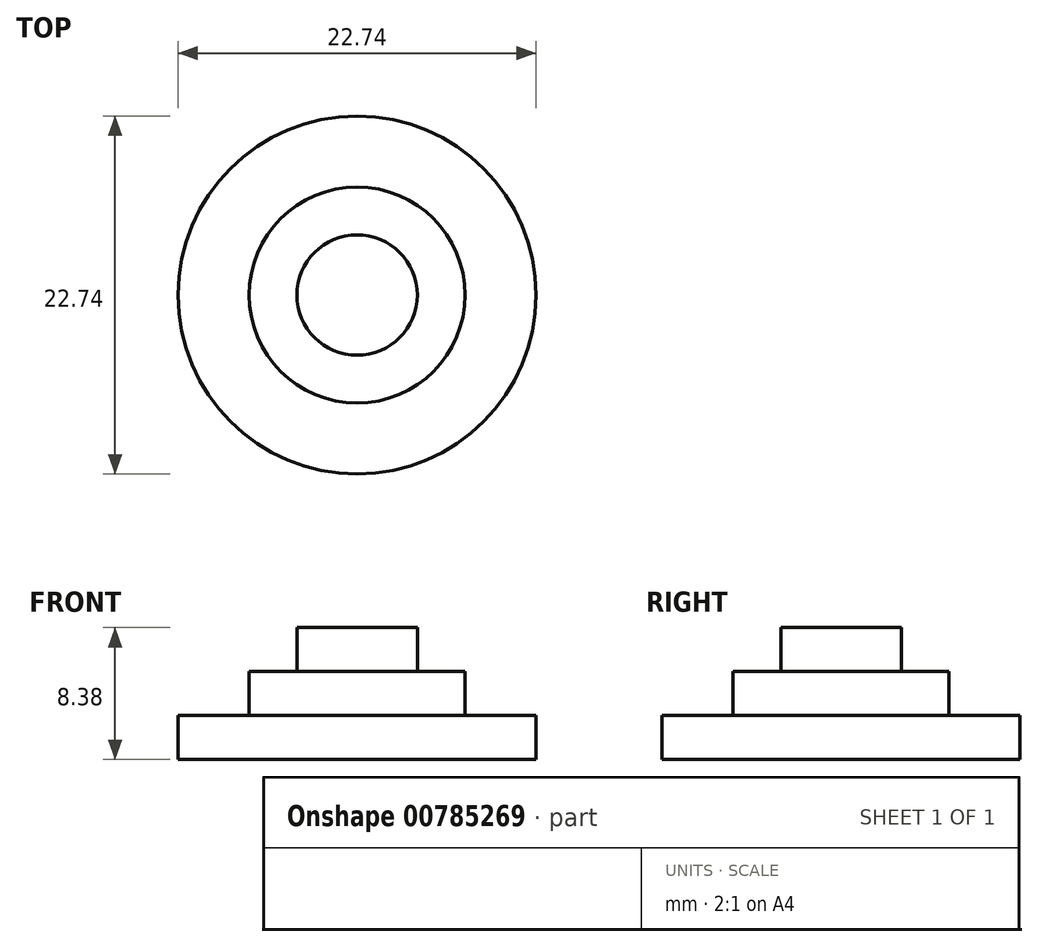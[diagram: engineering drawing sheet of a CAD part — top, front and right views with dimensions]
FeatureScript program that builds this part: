
annotation { "Feature Type Name" : "Feature", "Feature Type Description" : "" }
export const myFeature = defineFeature(function(context is Context, id is Id, definition is map)
    precondition{}
    {
        {
            var Q0;
            Q0=qCreatedBy(makeId("Top.planeOp"),FACE);
            var sketch = newSketch(context, id + "F0", { "sketchPlane" : qUnion([Q0])});
            skCircle(sketch, "E0", {"center": v(0, 0) * mm, "radius": 3.82 * mm});
            skCircle(sketch, "E1", {"center": v(0, 0) * mm, "radius": 6.86 * mm});
            skSolve(sketch);
        }
        {
            var Q0;
            Q0=makeQuery(id+"F0.imprint","IMPRINT",FACE,{"disambiguationData":[TD([[makeQuery(id+"F0.imprint","IMPRINT",EDGE,{"derivedFrom":sQuery(id+"F0.wireOp",EDGE,"E0")}),1.0]])]});
            extrude(context, id + "F1", {"entities" : qUnion([Q0]), "depth" : 2.8 * mm, "offsetDistance" : 25.4 * mm});
        }
        {
            var Q0;
            Q0=makeQuery(id+"F0.imprint","IMPRINT",FACE,{"disambiguationData":[TD([[makeQuery(id+"F0.imprint","IMPRINT",EDGE,{"derivedFrom":sQuery(id+"F0.wireOp",EDGE,"E0")}),-1.0]])]});
            var Q1;
            Q1=makeQuery(id+"F0.imprint","IMPRINT",FACE,{"disambiguationData":[TD([[makeQuery(id+"F0.imprint","IMPRINT",EDGE,{"derivedFrom":sQuery(id+"F0.wireOp",EDGE,"E0")}),1.0]])]});
            extrude(context, id + "F2", {"entities" : qUnion([Q0, Q1]), "operationType" : NewBodyOperationType.ADD, "oppositeDirection" : true, "depth" : 2.8 * mm, "offsetDistance" : 25.4 * mm});
        }
        {
            var Q0;
            Q0=makeQuery(id+"F2.opExtrude","CAP_FACE",FACE,{"disambiguationData":[OSD([sQuery(id+"F0.wireOp",EDGE,"E1")])],"isStart":false});
            var sketch = newSketch(context, id + "F3", { "sketchPlane" : qUnion([Q0])});
            skCircle(sketch, "E2", {"center": v(0, 0) * mm, "radius": 11.37 * mm});
            skSolve(sketch);
        }
        {
            var Q0;
            Q0=makeQuery(id+"F3.imprint","IMPRINT",FACE,{"disambiguationData":[TD([[makeQuery(id+"F3.imprint","IMPRINT",EDGE,{"derivedFrom":sQuery(id+"F3.wireOp",EDGE,"E2")}),1.0]])]});
            var Q1;
            Q1=makeQuery(id+"F3.imprint","IMPRINT",FACE,{"disambiguationData":[TD([[makeQuery(id+"F3.imprint","IMPRINT",EDGE,{"derivedFrom":makeQuery(id+"F2.opExtrude","CAP_EDGE",EDGE,{"disambiguationData":[OSD([sQuery(id+"F0.wireOp",EDGE,"E1")])],"isStart":false})}),-1.0]])]});
            extrude(context, id + "F4", {"entities" : qUnion([Q0, Q1]), "operationType" : NewBodyOperationType.ADD, "depth" : 2.8 * mm, "offsetDistance" : 25.4 * mm});
        }
    });
